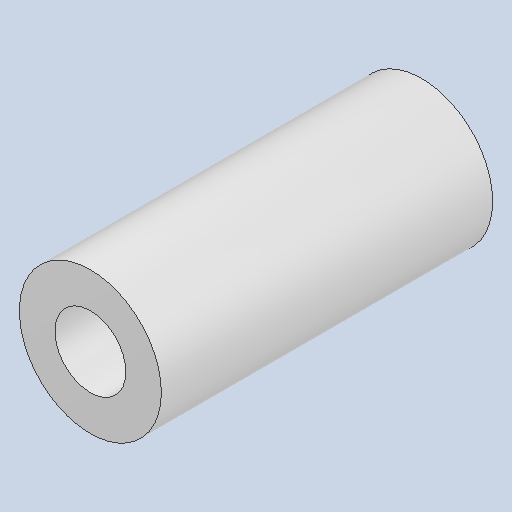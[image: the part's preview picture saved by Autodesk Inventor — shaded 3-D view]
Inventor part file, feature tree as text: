
AUTODESK INVENTOR PART (.ipt)
format: ipt  version: 2023 (Build 270158030, 158C)  size: 101,888 bytes
history: native  units: mm
features: extrude x1, sketch x1
ambient origin geometry x8: Origin, YZ Plane, XZ Plane, XY Plane, X Axis, Y Axis, Z Axis, Center Point
bodies: Solid1 (feature_tree)
feature tree (2):
  extrude  "Extrusion1"  Depth=14.0mm
  sketch  "Sketch1"  dims[d0=3.0mm d1=6.0mm d2=14.0mm d3=0.0mm]
